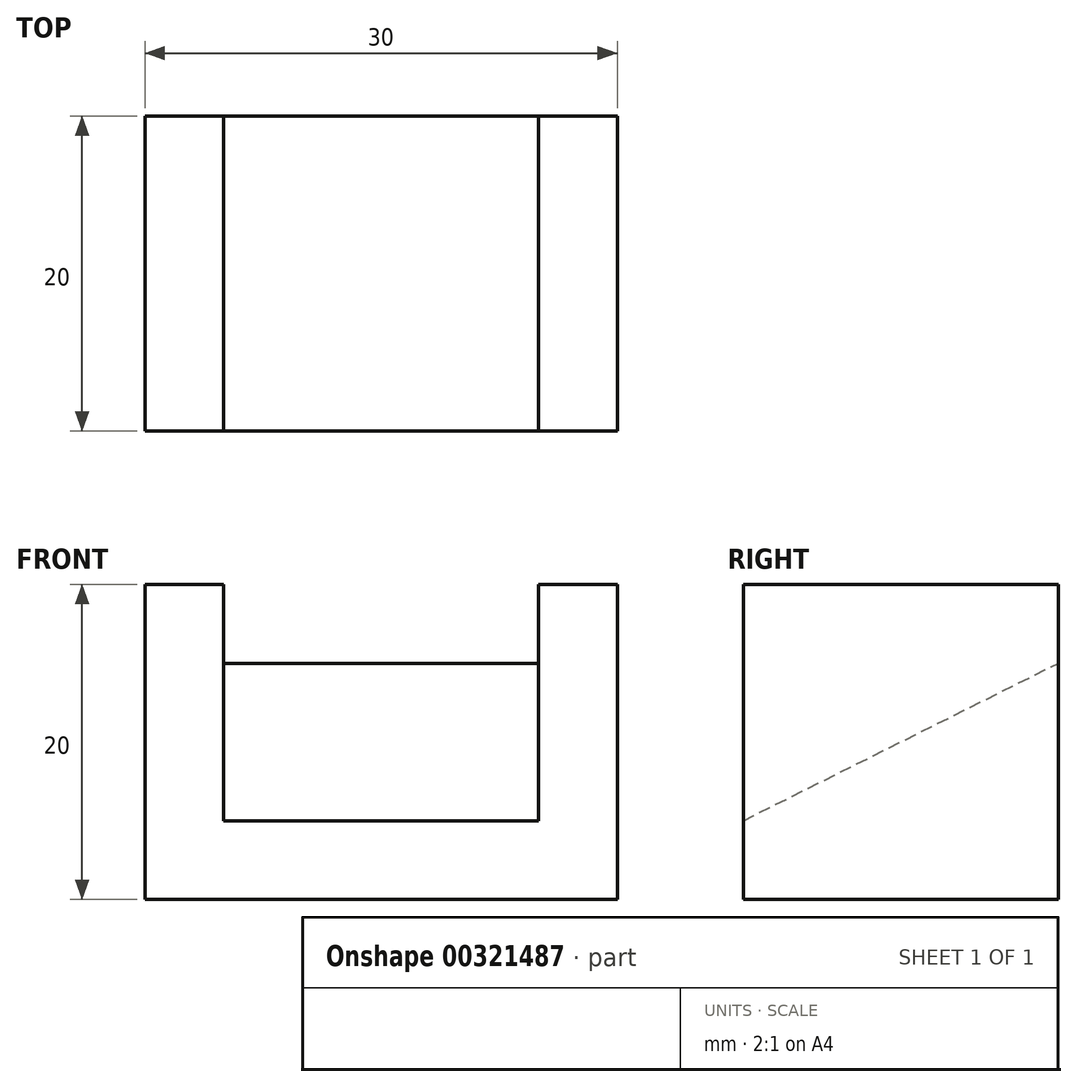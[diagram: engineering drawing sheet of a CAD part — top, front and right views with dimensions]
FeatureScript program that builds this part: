
annotation { "Feature Type Name" : "Feature", "Feature Type Description" : "" }
export const myFeature = defineFeature(function(context is Context, id is Id, definition is map)
    precondition{}
    {
        {
            var Q0;
            Q0=qCreatedBy(makeId("Right.planeOp"),FACE);
            var sketch = newSketch(context, id + "F0", { "sketchPlane" : qUnion([Q0])});
            skLineSegment(sketch, "E0", {"start": v(0, 0) * mm, "end": v(-20, 0) * mm});
            skLineSegment(sketch, "E1", {"start": v(-20, 0) * mm, "end": v(-20, 15) * mm});
            skLineSegment(sketch, "E2", {"start": v(-20, 15) * mm, "end": v(0, 15) * mm});
            skLineSegment(sketch, "E3", {"start": v(0, 15) * mm, "end": v(0, 0) * mm});
            skSolve(sketch);
        }
        {
            var Q0;
            Q0 = qSketchRegion(id + "F0", true);
            extrude(context, id + "F1", {"entities" : qUnion([Q0]), "depth" : 20 * mm});
        }
        {
            var Q0;
            Q0=makeQuery(id+"F1.opExtrude","CAP_FACE",FACE,{"disambiguationData":[OSD([sQuery(id+"F0.wireOp",EDGE,"E0"),sQuery(id+"F0.wireOp",EDGE,"E1"),sQuery(id+"F0.wireOp",EDGE,"E2"),sQuery(id+"F0.wireOp",EDGE,"E3")])],"isStart":false});
            var sketch = newSketch(context, id + "F2", { "sketchPlane" : qUnion([Q0])});
            skLineSegment(sketch, "E4", {"start": v(0, 15) * mm, "end": v(0, 0) * mm});
            skLineSegment(sketch, "E5", {"start": v(0, 0) * mm, "end": v(-20, 0) * mm});
            skLineSegment(sketch, "E6", {"start": v(-20, 0) * mm, "end": v(-20, 5) * mm});
            skLineSegment(sketch, "E7", {"start": v(-20, 5) * mm, "end": v(0, 15) * mm});
            skSolve(sketch);
        }
        {
            var Q0;
            {var subQ0=sQuery(id+"F2.wireOp",EDGE,"E7");Q0=makeQuery(id+"F2.imprint","IMPRINT",FACE,{"disambiguationData":[TD([[makeQuery(id+"F2.imprint","IMPRINT",EDGE,{"derivedFrom":subQ0}),1.0]])]});}
            extrude(context, id + "F3", {"entities" : qUnion([Q0]), "operationType" : NewBodyOperationType.REMOVE, "endBound" : BoundingType.THROUGH_ALL, "oppositeDirection" : true, "depth" : 25 * mm});
        }
        {
            var Q0;
            Q0=makeQuery(id+"F1.opExtrude","CAP_FACE",FACE,{"disambiguationData":[OSD([sQuery(id+"F0.wireOp",EDGE,"E0"),sQuery(id+"F0.wireOp",EDGE,"E1"),sQuery(id+"F0.wireOp",EDGE,"E2"),sQuery(id+"F0.wireOp",EDGE,"E3")])],"isStart":false});
            var sketch = newSketch(context, id + "F4", { "sketchPlane" : qUnion([Q0])});
            skLineSegment(sketch, "E8", {"start": v(-20, 0) * mm, "end": v(-20, 20) * mm});
            skLineSegment(sketch, "E9", {"start": v(-20, 20) * mm, "end": v(0, 20) * mm});
            skLineSegment(sketch, "E10", {"start": v(0, 20) * mm, "end": v(0, 0) * mm});
            skLineSegment(sketch, "E11", {"start": v(0, 0) * mm, "end": v(-20, 0) * mm});
            skSolve(sketch);
        }
        {
            var Q0;
            Q0 = qSketchRegion(id + "F4", true);
            extrude(context, id + "F5", {"entities" : qUnion([Q0]), "operationType" : NewBodyOperationType.ADD, "depth" : 5 * mm});
        }
        {
            var Q0;
            Q0=makeQuery(id+"F1.opExtrude","CAP_FACE",FACE,{"disambiguationData":[OSD([sQuery(id+"F0.wireOp",EDGE,"E0"),sQuery(id+"F0.wireOp",EDGE,"E1"),sQuery(id+"F0.wireOp",EDGE,"E2"),sQuery(id+"F0.wireOp",EDGE,"E3")])],"isStart":true});
            var sketch = newSketch(context, id + "F6", { "sketchPlane" : qUnion([Q0])});
            skLineSegment(sketch, "E12", {"start": v(0, 0) * mm, "end": v(0, 20) * mm});
            skLineSegment(sketch, "E13", {"start": v(0, 20) * mm, "end": v(20, 20) * mm});
            skLineSegment(sketch, "E14", {"start": v(20, 20) * mm, "end": v(20, 0) * mm});
            skLineSegment(sketch, "E15", {"start": v(20, 0) * mm, "end": v(0, 0) * mm});
            skSolve(sketch);
        }
        {
            var Q0;
            Q0 = qSketchRegion(id + "F6", true);
            extrude(context, id + "F7", {"entities" : qUnion([Q0]), "operationType" : NewBodyOperationType.ADD, "depth" : 5 * mm});
        }
    });
